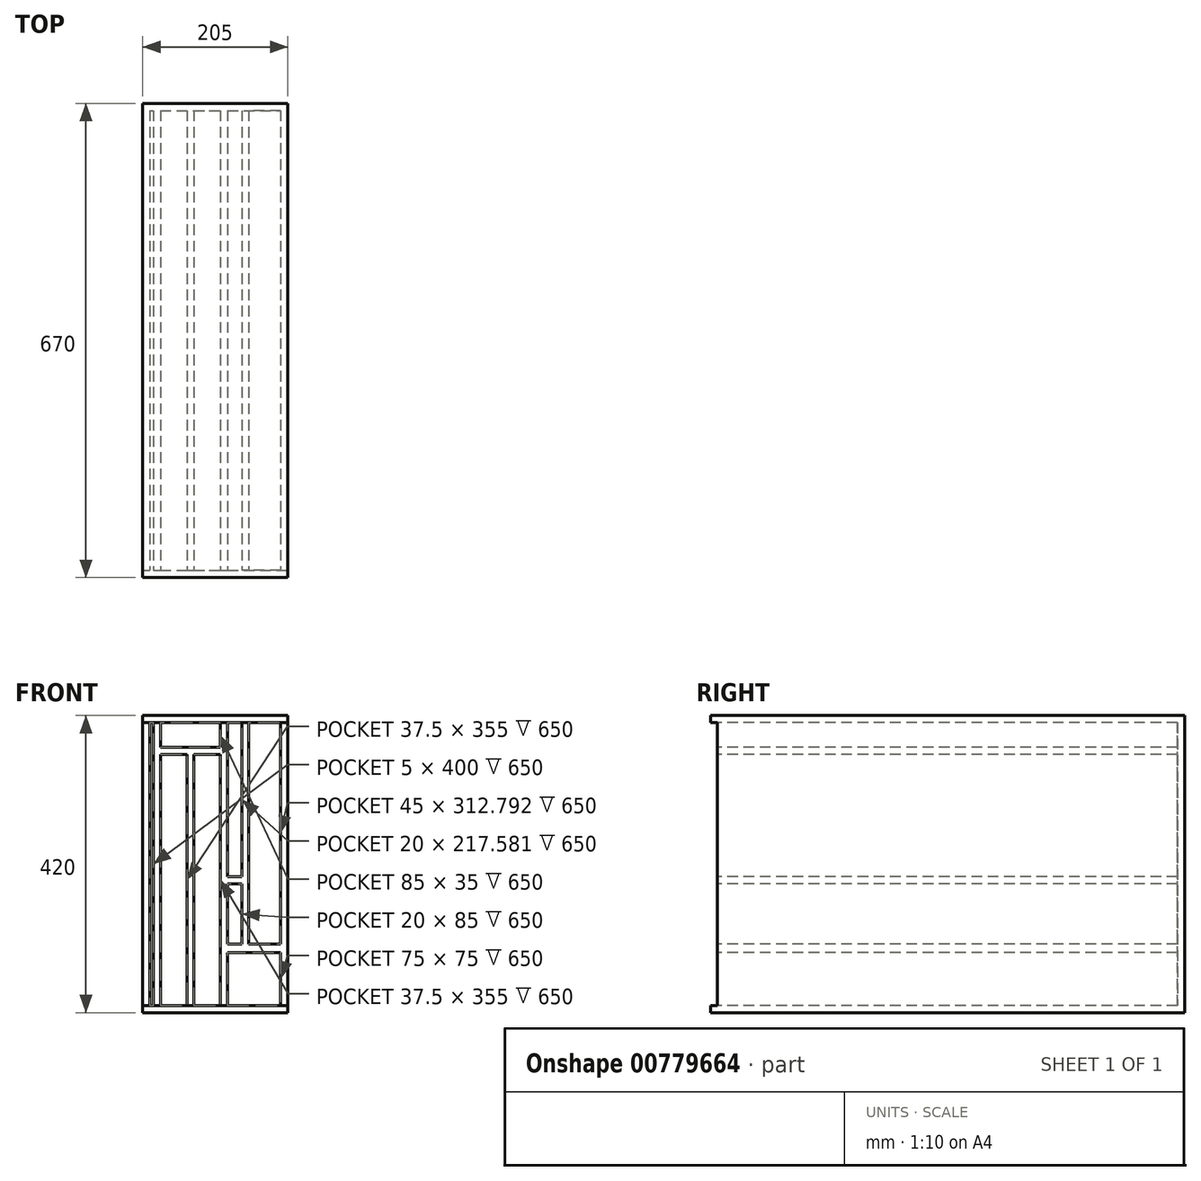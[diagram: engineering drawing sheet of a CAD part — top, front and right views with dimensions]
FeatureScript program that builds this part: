
annotation { "Feature Type Name" : "Feature", "Feature Type Description" : "" }
export const myFeature = defineFeature(function(context is Context, id is Id, definition is map)
    precondition{}
    {
        {
            var Q0;
            Q0=qCreatedBy(makeId("Front.planeOp"),FACE);
            var sketch = newSketch(context, id + "F0", { "sketchPlane" : qUnion([Q0])});
            skLineSegment(sketch, "E0.bottom", {"start": v(-418.51, 0) * mm, "end": v(-213.51, 0) * mm});
            skLineSegment(sketch, "E0.top", {"start": v(-418.51, 420) * mm, "end": v(-213.51, 420) * mm});
            skLineSegment(sketch, "E0.left", {"start": v(-418.51, 0) * mm, "end": v(-418.51, 420) * mm});
            skLineSegment(sketch, "E0.right", {"start": v(-213.51, 0) * mm, "end": v(-213.51, 420) * mm});
            skLineSegment(sketch, "E1.bottom", {"start": v(-408.51, 410) * mm, "end": v(-403.51, 410) * mm});
            skLineSegment(sketch, "E1.top", {"start": v(-408.51, 10) * mm, "end": v(-403.51, 10) * mm});
            skLineSegment(sketch, "E1.left", {"start": v(-408.51, 410) * mm, "end": v(-408.51, 10) * mm});
            skLineSegment(sketch, "E1.right", {"start": v(-403.51, 410) * mm, "end": v(-403.51, 10) * mm});
            skLineSegment(sketch, "E2.bottom", {"start": v(-393.51, 10) * mm, "end": v(-356.01, 10) * mm});
            skLineSegment(sketch, "E2.top", {"start": v(-393.51, 365) * mm, "end": v(-356.01, 365) * mm});
            skLineSegment(sketch, "E2.left", {"start": v(-393.51, 10) * mm, "end": v(-393.51, 365) * mm});
            skLineSegment(sketch, "E2.right", {"start": v(-356.01, 10) * mm, "end": v(-356.01, 365) * mm});
            skLineSegment(sketch, "E3.bottom", {"start": v(-346.01, 10) * mm, "end": v(-308.51, 10) * mm});
            skLineSegment(sketch, "E3.top", {"start": v(-346.01, 365) * mm, "end": v(-308.51, 365) * mm});
            skLineSegment(sketch, "E3.left", {"start": v(-346.01, 10) * mm, "end": v(-346.01, 365) * mm});
            skLineSegment(sketch, "E3.right", {"start": v(-308.51, 10) * mm, "end": v(-308.51, 365) * mm});
            skLineSegment(sketch, "E4.bottom", {"start": v(-298.51, 10) * mm, "end": v(-223.51, 10) * mm});
            skLineSegment(sketch, "E4.top", {"start": v(-298.51, 85) * mm, "end": v(-223.51, 85) * mm});
            skLineSegment(sketch, "E4.left", {"start": v(-298.51, 10) * mm, "end": v(-298.51, 85) * mm});
            skLineSegment(sketch, "E4.right", {"start": v(-223.51, 10) * mm, "end": v(-223.51, 85) * mm});
            skLineSegment(sketch, "E5.bottom", {"start": v(-298.51, 97.2) * mm, "end": v(-278.51, 97.2) * mm});
            skLineSegment(sketch, "E5.top", {"start": v(-298.51, 182.2) * mm, "end": v(-278.51, 182.2) * mm});
            skLineSegment(sketch, "E5.left", {"start": v(-298.51, 97.2) * mm, "end": v(-298.51, 182.2) * mm});
            skLineSegment(sketch, "E5.right", {"start": v(-278.51, 97.2) * mm, "end": v(-278.51, 182.2) * mm});
            skLineSegment(sketch, "E6.bottom", {"start": v(-393.51, 375) * mm, "end": v(-308.51, 375) * mm});
            skLineSegment(sketch, "E6.top", {"start": v(-393.51, 410) * mm, "end": v(-308.51, 410) * mm});
            skLineSegment(sketch, "E6.left", {"start": v(-393.51, 375) * mm, "end": v(-393.51, 410) * mm});
            skLineSegment(sketch, "E6.right", {"start": v(-308.51, 375) * mm, "end": v(-308.51, 410) * mm});
            skLineSegment(sketch, "E7.bottom", {"start": v(-298.51, 192.42) * mm, "end": v(-278.51, 192.42) * mm});
            skLineSegment(sketch, "E7.top", {"start": v(-298.51, 410) * mm, "end": v(-278.51, 410) * mm});
            skLineSegment(sketch, "E7.left", {"start": v(-298.51, 192.42) * mm, "end": v(-298.51, 410) * mm});
            skLineSegment(sketch, "E7.right", {"start": v(-278.51, 192.42) * mm, "end": v(-278.51, 410) * mm});
            skLineSegment(sketch, "E8.bottom", {"start": v(-223.51, 97.2) * mm, "end": v(-268.51, 97.2) * mm});
            skLineSegment(sketch, "E8.top", {"start": v(-223.51, 410) * mm, "end": v(-268.51, 410) * mm});
            skLineSegment(sketch, "E8.left", {"start": v(-223.51, 97.2) * mm, "end": v(-223.51, 410) * mm});
            skLineSegment(sketch, "E8.right", {"start": v(-268.51, 97.2) * mm, "end": v(-268.51, 410) * mm});
            skSolve(sketch);
        }
        {
            var Q0;
            Q0 = qSketchRegion(id + "F0", true);
            extrude(context, id + "F1", {"entities" : qUnion([Q0]), "oppositeDirection" : true, "depth" : 650 * mm, "offsetDistance" : 25.4 * mm});
        }
        {
            var Q0;
            Q0=makeQuery(id+"F1.opExtrude","SWEPT_FACE",FACE,{"disambiguationData":[OSD([sQuery(id+"F0.wireOp",EDGE,"E0.right")])]});
            var sketch = newSketch(context, id + "F2", { "sketchPlane" : qUnion([Q0])});
            skLineSegment(sketch, "E9.bottom", {"start": v(650, 420) * mm, "end": v(660, 420) * mm});
            skLineSegment(sketch, "E9.top", {"start": v(650, 0) * mm, "end": v(660, 0) * mm});
            skLineSegment(sketch, "E9.left", {"start": v(650, 420) * mm, "end": v(650, 0) * mm});
            skLineSegment(sketch, "E9.right", {"start": v(660, 420) * mm, "end": v(660, 0) * mm});
            skSolve(sketch);
        }
        {
            var Q0;
            Q0 = qSketchRegion(id + "F2", true);
            var Q1;
            Q1=makeQuery(id+"F1.opExtrude","SWEPT_FACE",FACE,{"disambiguationData":[OSD([sQuery(id+"F0.wireOp",EDGE,"E0.left")])]});
            extrude(context, id + "F3", {"entities" : qUnion([Q0]), "operationType" : NewBodyOperationType.ADD, "endBound" : BoundingType.UP_TO_SURFACE, "oppositeDirection" : true, "depth" : 25.4 * mm, "endBoundEntityFace" : qUnion([Q1]), "offsetDistance" : 25.4 * mm});
        }
        {
            var Q0;
            Q0=makeQuery(id+"F1.opExtrude","CAP_FACE",FACE,{"disambiguationData":[OSD([sQuery(id+"F0.wireOp",EDGE,"E0.bottom"),sQuery(id+"F0.wireOp",EDGE,"E0.top"),sQuery(id+"F0.wireOp",EDGE,"E0.left"),sQuery(id+"F0.wireOp",EDGE,"E0.right"),sQuery(id+"F0.wireOp",EDGE,"E1.bottom"),sQuery(id+"F0.wireOp",EDGE,"E1.top"),sQuery(id+"F0.wireOp",EDGE,"E1.left"),sQuery(id+"F0.wireOp",EDGE,"E1.right"),sQuery(id+"F0.wireOp",EDGE,"E2.bottom"),sQuery(id+"F0.wireOp",EDGE,"E2.top"),sQuery(id+"F0.wireOp",EDGE,"E2.left"),sQuery(id+"F0.wireOp",EDGE,"E2.right"),sQuery(id+"F0.wireOp",EDGE,"E3.bottom"),sQuery(id+"F0.wireOp",EDGE,"E3.top"),sQuery(id+"F0.wireOp",EDGE,"E3.left"),sQuery(id+"F0.wireOp",EDGE,"E3.right"),sQuery(id+"F0.wireOp",EDGE,"E4.bottom"),sQuery(id+"F0.wireOp",EDGE,"E4.top"),sQuery(id+"F0.wireOp",EDGE,"E4.left"),sQuery(id+"F0.wireOp",EDGE,"E4.right"),sQuery(id+"F0.wireOp",EDGE,"E5.bottom"),sQuery(id+"F0.wireOp",EDGE,"E5.top"),sQuery(id+"F0.wireOp",EDGE,"E5.left"),sQuery(id+"F0.wireOp",EDGE,"E5.right"),sQuery(id+"F0.wireOp",EDGE,"E6.bottom"),sQuery(id+"F0.wireOp",EDGE,"E6.top"),sQuery(id+"F0.wireOp",EDGE,"E6.left"),sQuery(id+"F0.wireOp",EDGE,"E6.right"),sQuery(id+"F0.wireOp",EDGE,"E7.bottom"),sQuery(id+"F0.wireOp",EDGE,"E7.top"),sQuery(id+"F0.wireOp",EDGE,"E7.left"),sQuery(id+"F0.wireOp",EDGE,"E7.right"),sQuery(id+"F0.wireOp",EDGE,"E8.bottom"),sQuery(id+"F0.wireOp",EDGE,"E8.top"),sQuery(id+"F0.wireOp",EDGE,"E8.left"),sQuery(id+"F0.wireOp",EDGE,"E8.right")])],"isStart":true});
            var sketch = newSketch(context, id + "F4", { "sketchPlane" : qUnion([Q0])});
            skPoint(sketch, "E10.oppositeSnap0", {"position": v(-288.51, 410) * mm});
            skLineSegment(sketch, "E10.bottom", {"start": v(-418.51, 420) * mm, "end": v(-213.51, 420) * mm});
            skLineSegment(sketch, "E10.top", {"start": v(-418.51, 410) * mm, "end": v(-213.51, 410) * mm});
            skLineSegment(sketch, "E10.left", {"start": v(-418.51, 420) * mm, "end": v(-418.51, 410) * mm});
            skLineSegment(sketch, "E10.right", {"start": v(-213.51, 420) * mm, "end": v(-213.51, 410) * mm});
            skLineSegment(sketch, "E11.bottom", {"start": v(-213.51, 0) * mm, "end": v(-418.51, 0) * mm});
            skLineSegment(sketch, "E11.top", {"start": v(-213.51, 10) * mm, "end": v(-418.51, 10) * mm});
            skLineSegment(sketch, "E11.left", {"start": v(-213.51, 0) * mm, "end": v(-213.51, 10) * mm});
            skLineSegment(sketch, "E11.right", {"start": v(-418.51, 0) * mm, "end": v(-418.51, 10) * mm});
            skSolve(sketch);
        }
        {
            var Q0;
            Q0 = qSketchRegion(id + "F4", true);
            extrude(context, id + "F5", {"entities" : qUnion([Q0]), "operationType" : NewBodyOperationType.ADD, "depth" : 10 * mm, "offsetDistance" : 25.4 * mm});
        }
    });
